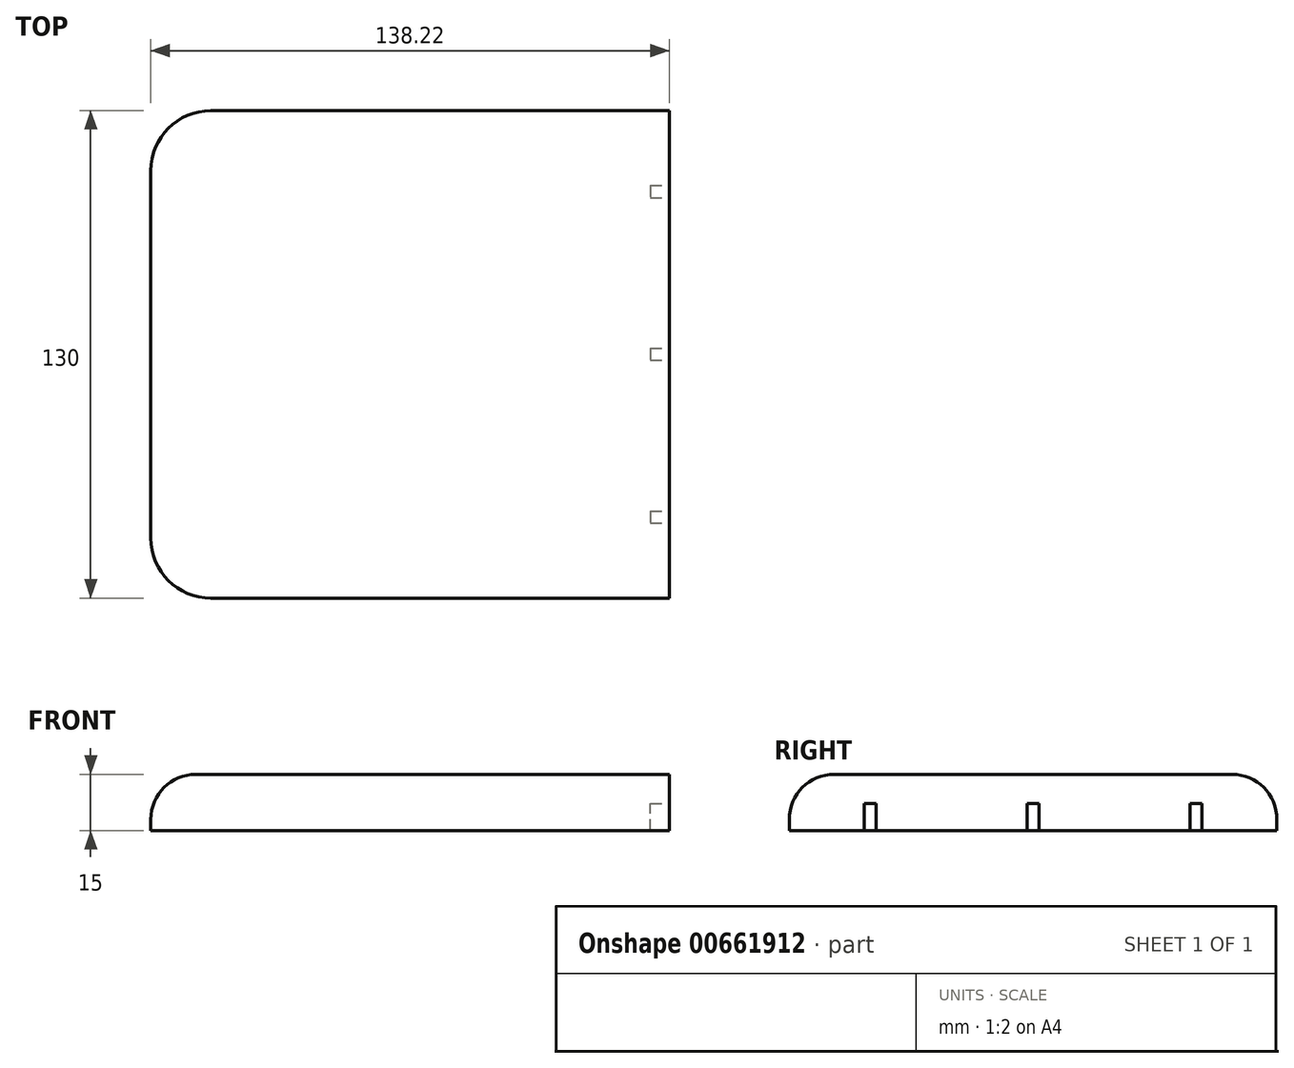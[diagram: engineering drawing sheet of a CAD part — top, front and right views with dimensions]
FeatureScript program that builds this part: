
annotation { "Feature Type Name" : "Feature", "Feature Type Description" : "" }
export const myFeature = defineFeature(function(context is Context, id is Id, definition is map)
    precondition{}
    {
        {
            var Q0;
            Q0=qCreatedBy(makeId("Top.planeOp"),FACE);
            var sketch = newSketch(context, id + "F0", { "sketchPlane" : qUnion([Q0])});
            skLineSegment(sketch, "E0.bottom", {"start": v(60.22, 65) * mm, "end": v(-78, 65) * mm});
            skLineSegment(sketch, "E0.top", {"start": v(60.22, -65) * mm, "end": v(-78, -65) * mm});
            skLineSegment(sketch, "E0.right", {"start": v(-78, 65) * mm, "end": v(-78, -65) * mm});
            skPoint(sketch, "E0.middle", {"position": v(0, 0) * mm});
            skLineSegment(sketch, "E1", {"start": v(60.22, 65) * mm, "end": v(60.22, -65) * mm});
            skSolve(sketch);
        }
        {
            var Q0;
            Q0=qSketchRegion(id+"F0",true);
            extrude(context, id + "F1", {"entities" : qUnion([Q0]), "depth" : 25 * mm, "offsetDistance" : 25 * mm});
        }
        {
            var Q0;
            Q0=makeQuery(id+"F1.opExtrude","SWEPT_EDGE",EDGE,{"disambiguationData":[OSD([sQuery(id+"F0.wireOp",EDGE,"E0.top"),sQuery(id+"F0.wireOp",EDGE,"E0.right")])]});
            var Q1;
            Q1=makeQuery(id+"F1.opExtrude","SWEPT_EDGE",EDGE,{"disambiguationData":[OSD([sQuery(id+"F0.wireOp",EDGE,"E0.bottom"),sQuery(id+"F0.wireOp",EDGE,"E0.right")])]});
            fillet(context, id + "F2", {"entities" : qUnion([Q0, Q1]), "radius" : 16 * mm, "tangentPropagation" : true, "allowEdgeOverflow" : false});
        }
        {
            var Q0;
            Q0=makeQuery(id+"F1.opExtrude","CAP_EDGE",EDGE,{"disambiguationData":[OSD([sQuery(id+"F0.wireOp",EDGE,"E0.top")])],"isStart":false});
            fillet(context, id + "F3", {"entities" : qUnion([Q0]), "radius" : 12 * mm, "tangentPropagation" : true, "allowEdgeOverflow" : false});
        }
        {
            var Q0;
            Q0=makeQuery(id+"F1.opExtrude","CAP_FACE",FACE,{"disambiguationData":[OSD([sQuery(id+"F0.wireOp",EDGE,"E0.bottom"),sQuery(id+"F0.wireOp",EDGE,"E0.top"),sQuery(id+"F0.wireOp",EDGE,"E0.right"),sQuery(id+"F0.wireOp",EDGE,"E1")])],"isStart":true});
            extrude(context, id + "F4", {"entities" : qUnion([Q0]), "operationType" : NewBodyOperationType.REMOVE, "oppositeDirection" : true, "depth" : 10 * mm, "offsetDistance" : 25 * mm});
        }
        {
            var Q0;
            Q0=makeQuery(id+"F1.opExtrude","SWEPT_FACE",FACE,{"disambiguationData":[OSD([sQuery(id+"F0.wireOp",EDGE,"E1")])]});
            var sketch = newSketch(context, id + "F5", { "sketchPlane" : qUnion([Q0])});
            skLineSegment(sketch, "E2.bottom", {"start": v(0, 10) * mm, "end": v(1.6, 10) * mm});
            skLineSegment(sketch, "E2.top", {"start": v(0, 17.2) * mm, "end": v(1.6, 17.2) * mm});
            skLineSegment(sketch, "E2.right", {"start": v(1.6, 10) * mm, "end": v(1.6, 17.2) * mm});
            skLineSegment(sketch, "E3.bottom", {"start": v(0, 17.2) * mm, "end": v(-1.6, 17.2) * mm});
            skLineSegment(sketch, "E3.top", {"start": v(0, 10) * mm, "end": v(-1.6, 10) * mm});
            skLineSegment(sketch, "E3.right", {"start": v(-1.6, 17.2) * mm, "end": v(-1.6, 10) * mm});
            skLineSegment(sketch, "E4.bottom", {"start": v(45, 10) * mm, "end": v(41.8, 10) * mm});
            skLineSegment(sketch, "E4.top", {"start": v(45, 17.2) * mm, "end": v(41.8, 17.2) * mm});
            skLineSegment(sketch, "E4.left", {"start": v(45, 10) * mm, "end": v(45, 17.2) * mm});
            skLineSegment(sketch, "E4.right", {"start": v(41.8, 10) * mm, "end": v(41.8, 17.2) * mm});
            skLineSegment(sketch, "E5.bottom", {"start": v(-45, 10) * mm, "end": v(-41.8, 10) * mm});
            skLineSegment(sketch, "E5.top", {"start": v(-45, 17.2) * mm, "end": v(-41.8, 17.2) * mm});
            skLineSegment(sketch, "E5.left", {"start": v(-45, 10) * mm, "end": v(-45, 17.2) * mm});
            skLineSegment(sketch, "E5.right", {"start": v(-41.8, 10) * mm, "end": v(-41.8, 17.2) * mm});
            skSolve(sketch);
        }
        {
            var Q0;
            Q0=makeQuery(id+"F5.imprint","IMPRINT",FACE,{"disambiguationData":[TD([[makeQuery(id+"F5.imprint","IMPRINT",EDGE,{"derivedFrom":sQuery(id+"F5.wireOp",EDGE,"E5.bottom")}),-1.0]])]});
            var Q1;
            Q1=makeQuery(id+"F5.imprint","IMPRINT",FACE,{"disambiguationData":[TD([[makeQuery(id+"F5.imprint","IMPRINT",EDGE,{"derivedFrom":sQuery(id+"F5.wireOp",EDGE,"E2.bottom")}),-1.0]])]});
            var Q2;
            Q2=makeQuery(id+"F5.imprint","IMPRINT",FACE,{"disambiguationData":[TD([[makeQuery(id+"F5.imprint","IMPRINT",EDGE,{"derivedFrom":sQuery(id+"F5.wireOp",EDGE,"E4.bottom")}),-1.0]])]});
            extrude(context, id + "F6", {"entities" : qUnion([Q0, Q1, Q2]), "operationType" : NewBodyOperationType.REMOVE, "oppositeDirection" : true, "depth" : 5 * mm, "offsetDistance" : 25 * mm});
        }
    });
